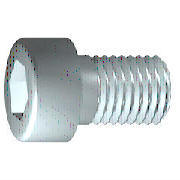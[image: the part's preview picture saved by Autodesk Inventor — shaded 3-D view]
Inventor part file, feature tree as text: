
AUTODESK INVENTOR PART (.ipt)
format: ipt  version: 2015 (Build 190159000, 159)  size: 198,656 bytes
history: native  units: mm (DEFAULTED — no unit token found)
features: sketch x2, extrude x1, plane x1, fillet x1
ambient origin geometry x7: Origin, YZ Plane, XY Plane, X Axis, Y Axis, Z Axis, Center Point
bodies: Solid1 (feature_tree), Body (feature_tree)
feature tree (5):
  extrude  "Slot"  Depth=5.0mm
  plane  "Work Plane1"
  fillet  "Fillet2"  Radius=5.0mm
  sketch  "Sketch1"  dims[d1=10.0mm d2=0.49086mm d3=5.0mm]
  sketch  "Sketch2"  dims[d4=2.5mm d5=60.0deg d6=5.0mm d7=5.0mm d8=4.618802mm d9=8.5mm d10=90.0deg d11=10.0mm d12=0.0mm d13=10.0mm d14=0.0mm d15=0.49076mm d16=0.49076mm d17=0.5mm d19=0.0mm d26=12.0mm d27=45.0deg d28=0.0mm d29=0.0mm d30=0.1mm]
